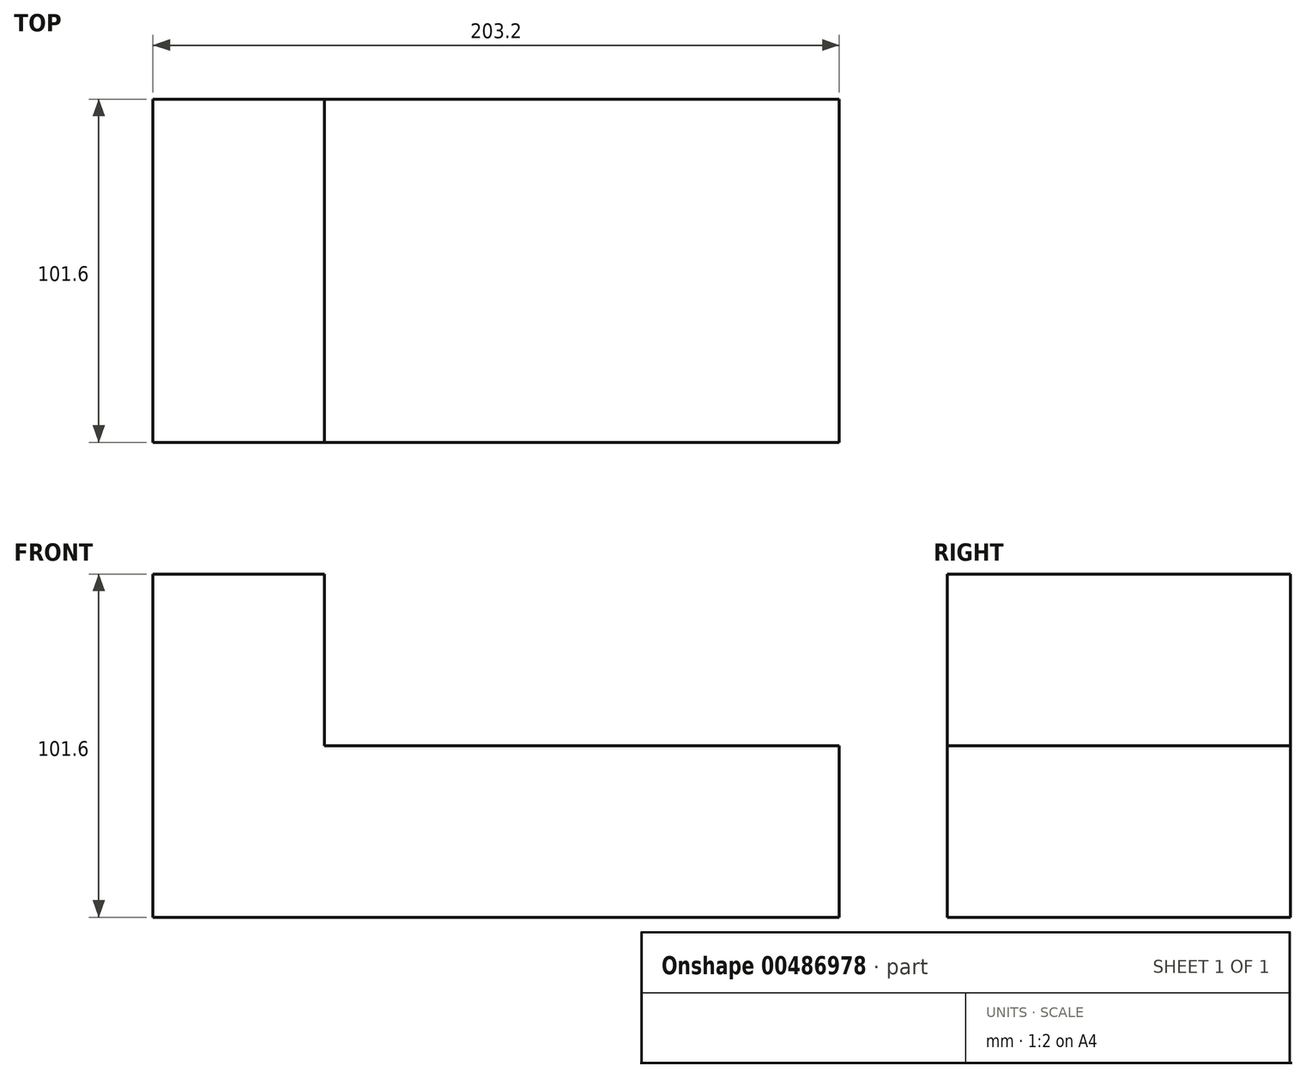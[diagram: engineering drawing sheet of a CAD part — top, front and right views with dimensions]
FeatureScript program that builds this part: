
annotation { "Feature Type Name" : "Feature", "Feature Type Description" : "" }
export const myFeature = defineFeature(function(context is Context, id is Id, definition is map)
    precondition{}
    {
        {
            var Q0;
            Q0=qCreatedBy(makeId("Top.planeOp"),FACE);
            var sketch = newSketch(context, id + "F0", { "sketchPlane" : qUnion([Q0])});
            skLineSegment(sketch, "E0.bottom", {"start": v(-93.03, 40.77) * mm, "end": v(110.17, 40.77) * mm});
            skLineSegment(sketch, "E0.top", {"start": v(-93.03, -60.83) * mm, "end": v(110.17, -60.83) * mm});
            skLineSegment(sketch, "E0.left", {"start": v(-93.03, 40.77) * mm, "end": v(-93.03, -60.83) * mm});
            skLineSegment(sketch, "E0.right", {"start": v(110.17, 40.77) * mm, "end": v(110.17, -60.83) * mm});
            skSolve(sketch);
        }
        {
            var Q0;
            Q0=makeQuery(id+"F0.imprint","IMPRINT",FACE,{"disambiguationData":[TD([[makeQuery(id+"F0.imprint","IMPRINT",EDGE,{"derivedFrom":sQuery(id+"F0.wireOp",EDGE,"E0.bottom")}),-1.0]])]});
            extrude(context, id + "F1", {"entities" : qUnion([Q0]), "depth" : 50.8 * mm});
        }
        {
            var Q0;
            Q0=makeQuery(id+"F1.opExtrude","SWEPT_FACE",FACE,{"disambiguationData":[OSD([sQuery(id+"F0.wireOp",EDGE,"E0.bottom")])]});
            var sketch = newSketch(context, id + "F2", { "sketchPlane" : qUnion([Q0])});
            skLineSegment(sketch, "E1.bottom", {"start": v(-110.17, 50.8) * mm, "end": v(-59.37, 50.8) * mm});
            skLineSegment(sketch, "E1.top", {"start": v(-110.17, 101.6) * mm, "end": v(-59.37, 101.6) * mm});
            skLineSegment(sketch, "E1.left", {"start": v(-110.17, 50.8) * mm, "end": v(-110.17, 101.6) * mm});
            skLineSegment(sketch, "E1.right", {"start": v(-59.37, 50.8) * mm, "end": v(-59.37, 101.6) * mm});
            skSolve(sketch);
        }
        {
            var Q0;
            Q0=makeQuery(id+"F2.imprint","IMPRINT",FACE,{"disambiguationData":[TD([[makeQuery(id+"F2.imprint","IMPRINT",EDGE,{"derivedFrom":sQuery(id+"F2.wireOp",EDGE,"E1.bottom")}),-1.0]])]});
            extrude(context, id + "F3", {"entities" : qUnion([Q0]), "operationType" : NewBodyOperationType.ADD, "oppositeDirection" : true, "depth" : 101.6 * mm});
        }
        {
            var Q0;
            Q0=makeQuery(id+"F1.opExtrude","SWEPT_BODY",BODY,{"disambiguationData":[OSD([sQuery(id+"F0.wireOp",EDGE,"E0.bottom"),sQuery(id+"F0.wireOp",EDGE,"E0.top"),sQuery(id+"F0.wireOp",EDGE,"E0.left"),sQuery(id+"F0.wireOp",EDGE,"E0.right")])]});
            var Q1;
            Q1=makeQuery(id+"F3.boolean.opBoolean","MERGE",EDGE,{"derivedFrom":[makeQuery(id+"F1.opExtrude","SWEPT_EDGE",EDGE,{"disambiguationData":[OSD([sQuery(id+"F0.wireOp",EDGE,"E0.top"),sQuery(id+"F0.wireOp",EDGE,"E0.right")])]}),makeQuery(id+"F3.opExtrude","CAP_EDGE",EDGE,{"disambiguationData":[OSD([sQuery(id+"F2.wireOp",EDGE,"E1.left")])],"isStart":false})]});
            transform(context, id + "F4", {"entities" : qUnion([Q0]), "transformType" : TransformType.ROTATION, "transformAxis" : qUnion([Q1]), "angle" : 180 * degree, "makeCopy" : false});
        }
    });
